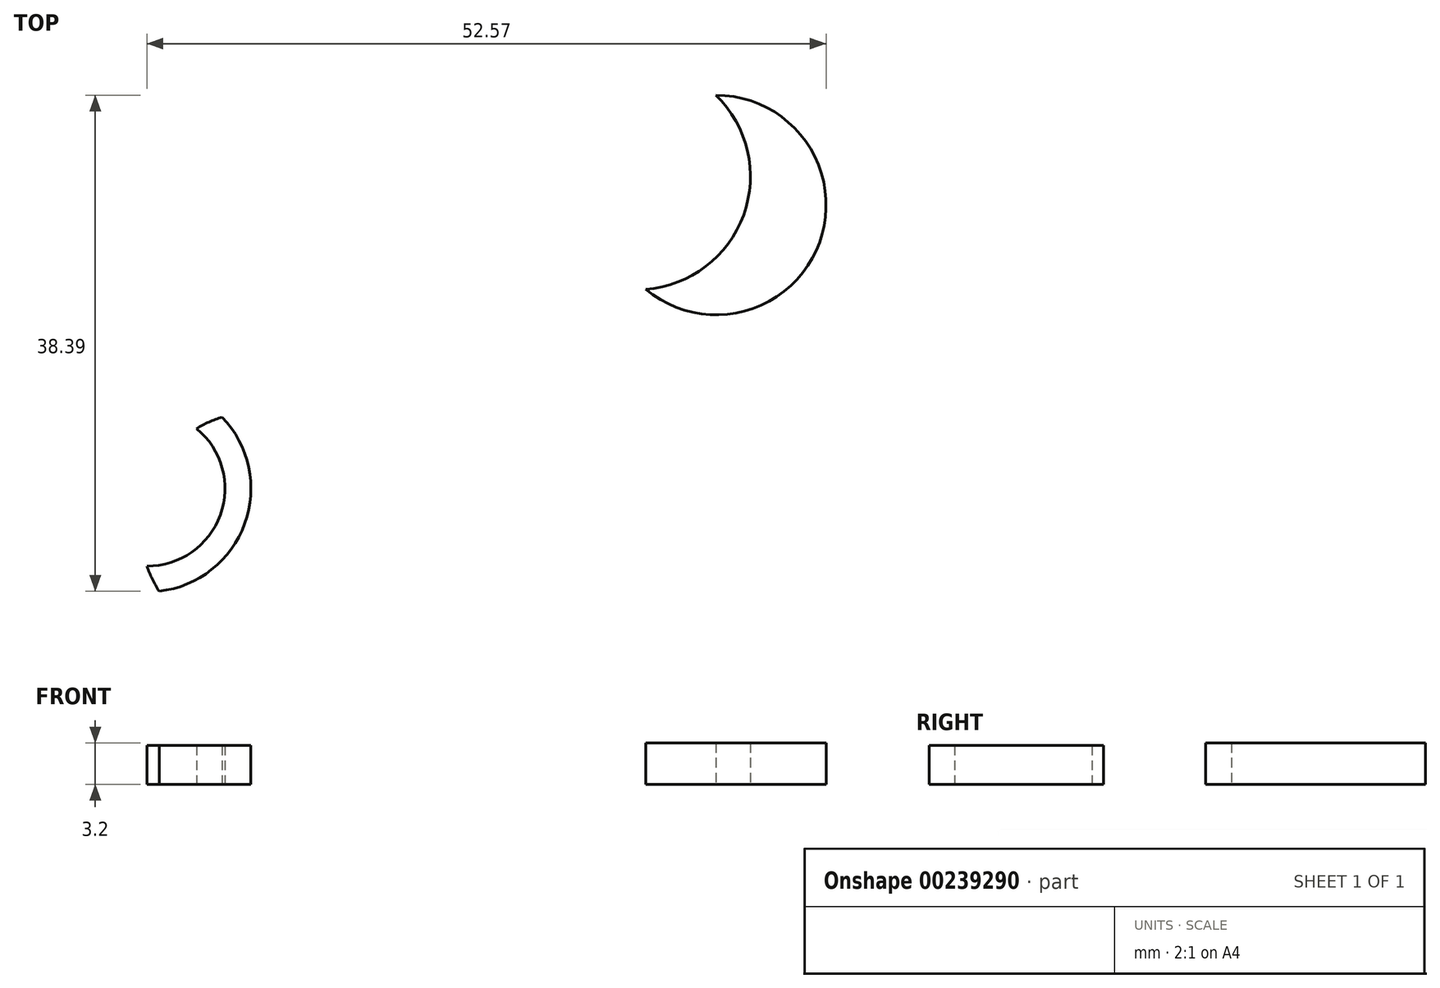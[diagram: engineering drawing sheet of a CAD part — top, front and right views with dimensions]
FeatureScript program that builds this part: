
annotation { "Feature Type Name" : "Feature", "Feature Type Description" : "" }
export const myFeature = defineFeature(function(context is Context, id is Id, definition is map)
    precondition{}
    {
        {
            var Q0;
            Q0=qCreatedBy(makeId("Top.planeOp"),FACE);
            var sketch = newSketch(context, id + "F0", { "sketchPlane" : qUnion([Q0])});
            skPoint(sketch, "E0", {"position": v(-46.4, 36.81) * mm});
            skCircle(sketch, "E1", {"center": v(-46.4, 36.81) * mm, "radius": 8.9 * mm});
            skLineSegment(sketch, "E2.bottom", {"start": v(-52.4, 45.81) * mm, "end": v(-40.4, 45.81) * mm});
            skLineSegment(sketch, "E2.top", {"start": v(-52.4, 36.81) * mm, "end": v(-40.4, 36.81) * mm});
            skLineSegment(sketch, "E2.left", {"start": v(-52.4, 45.81) * mm, "end": v(-52.4, 36.81) * mm});
            skLineSegment(sketch, "E2.right", {"start": v(-40.4, 45.81) * mm, "end": v(-40.4, 36.81) * mm});
            skLineSegment(sketch, "E3", {"start": v(-46.4, 36.81) * mm, "end": v(-46.4, 0) * mm});
            skPoint(sketch, "E4", {"position": v(-46.4, 34.81) * mm});
            skCircle(sketch, "E5", {"center": v(-46.4, 34.81) * mm, "radius": 6.1 * mm});
            skSolve(sketch);
        }
        {
            var Q0;
            {var subQ0=sQuery(id+"F0.wireOp",EDGE,"E2.left");var subQ3=sQuery(id+"F0.wireOp",EDGE,"E1");var subQ4=makeQuery(id+"F0.imprint","INTERSECT",VERTEX,{"derivedFrom":[subQ3,subQ0]});Q0=makeQuery(id+"F0.imprint","IMPRINT",FACE,{"disambiguationData":[TD([[makeQuery(id+"F0.imprint","IMPRINT",EDGE,{"disambiguationData":[TD([[subQ4,1.0]])],"derivedFrom":subQ3}),1.0]])]});}
            extrude(context, id + "F1", {"entities" : qUnion([Q0]), "depth" : 3 * mm});
        }
        {
            var Q0;
            Q0=qCreatedBy(makeId("Top.planeOp"),FACE);
            var sketch = newSketch(context, id + "F2", { "sketchPlane" : qUnion([Q0])});
            skCircle(sketch, "E6", {"center": v(-32.27, -26.2) * mm, "radius": 9 * mm});
            skCircle(sketch, "E7", {"center": v(-40.74, -23.13) * mm, "radius": 6 * mm});
            skCircle(sketch, "E8", {"center": v(-40.74, -23.13) * mm, "radius": 8 * mm});
            skSolve(sketch);
        }
        {
            var Q0;
            Q0=qCreatedBy(makeId("Top.planeOp"),FACE);
            var sketch = newSketch(context, id + "F3", { "sketchPlane" : qUnion([Q0])});
            skCircle(sketch, "E9", {"center": v(3.3, -1.19) * mm, "radius": 8.5 * mm});
            skCircle(sketch, "E10", {"center": v(-2.82, 1.02) * mm, "radius": 6 * mm});
            skCircle(sketch, "E11", {"center": v(-2.82, 1.02) * mm, "radius": 8.75 * mm});
            skSolve(sketch);
        }
        {
            var Q0;
            Q0=makeQuery(id+"F1.opExtrude","SWEPT_BODY",BODY,{"disambiguationData":[OSD([sQuery(id+"F0.wireOp",EDGE,"E1"),sQuery(id+"F0.wireOp",EDGE,"E2.top"),sQuery(id+"F0.wireOp",EDGE,"E2.left"),sQuery(id+"F0.wireOp",EDGE,"E2.right"),sQuery(id+"F0.wireOp",EDGE,"E5")])]});
            deleteBodies(context, id + "F4", {"entities" : qUnion([Q0])});
        }
        {
            var Q0;
            {var subQ0=sQuery(id+"F2.wireOp",EDGE,"E8");var subQ1=sQuery(id+"F2.wireOp",EDGE,"E6");var subQ2=makeQuery(id+"F2.imprint","INTERSECT",VERTEX,{"disambiguationData":[OD(0.0)],"derivedFrom":[subQ1,subQ0]});Q0=makeQuery(id+"F2.imprint","IMPRINT",FACE,{"disambiguationData":[TD([[makeQuery(id+"F2.imprint","IMPRINT",EDGE,{"disambiguationData":[TD([[subQ2,-1.0]])],"derivedFrom":subQ1}),1.0]])]});}
            extrude(context, id + "F5", {"entities" : qUnion([Q0]), "depth" : 3 * mm});
        }
        {
            var Q0;
            {var subQ0=sQuery(id+"F3.wireOp",EDGE,"E11");var subQ1=sQuery(id+"F3.wireOp",EDGE,"E9");var subQ2=makeQuery(id+"F3.imprint","INTERSECT",VERTEX,{"disambiguationData":[OD(0.0)],"derivedFrom":[subQ1,subQ0]});Q0=makeQuery(id+"F3.imprint","IMPRINT",FACE,{"disambiguationData":[TD([[makeQuery(id+"F3.imprint","IMPRINT",EDGE,{"disambiguationData":[TD([[subQ2,1.0]])],"derivedFrom":subQ1}),1.0]])]});}
            extrude(context, id + "F6", {"entities" : qUnion([Q0]), "depth" : 3.2 * mm});
        }
    });
